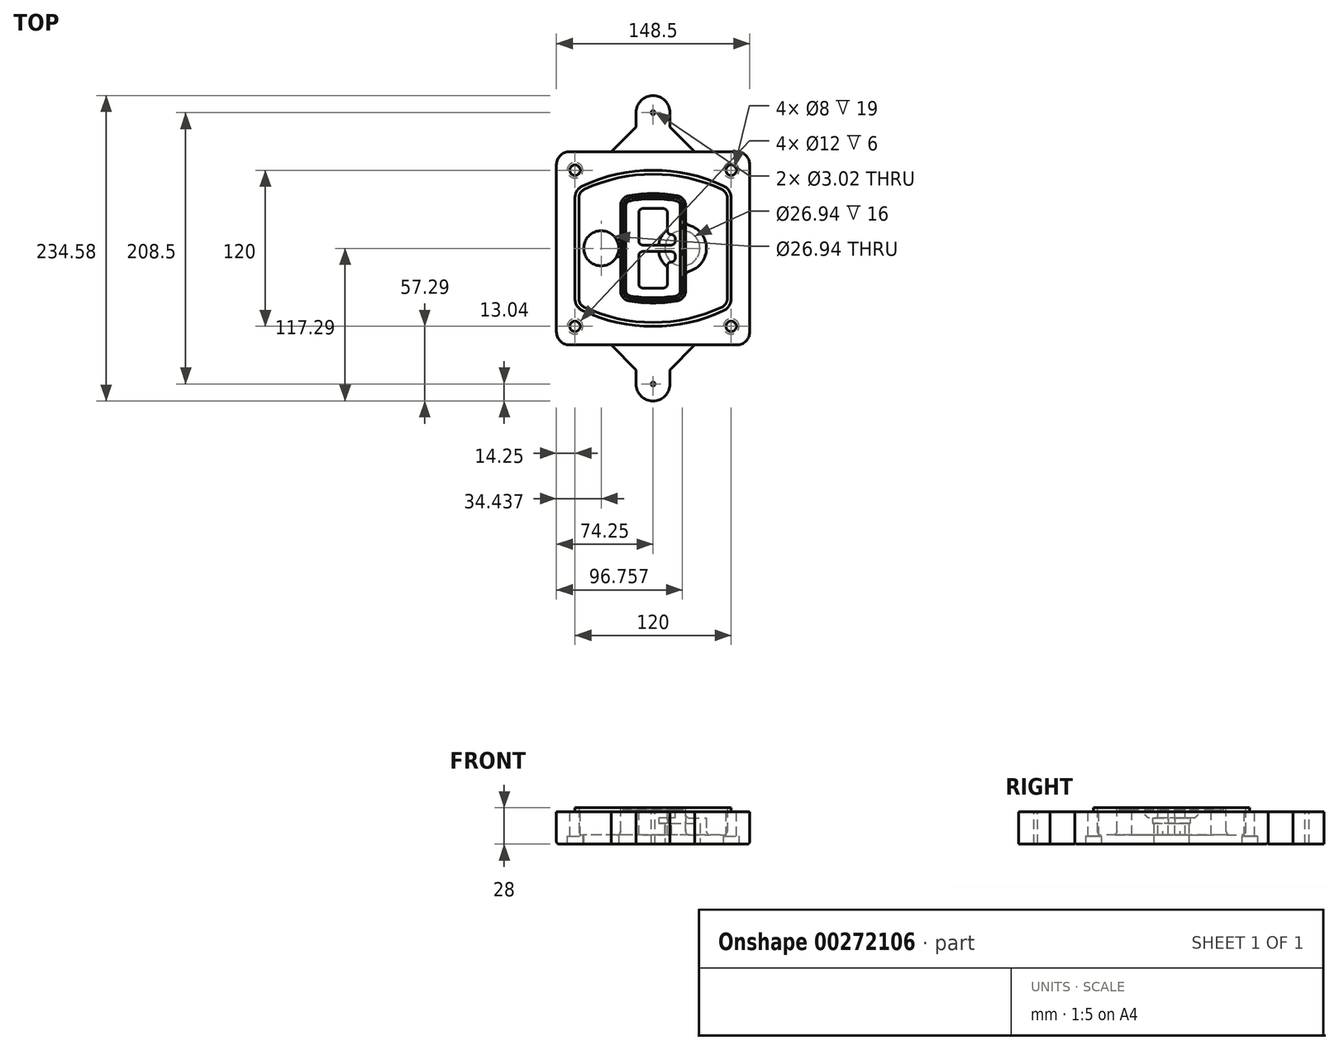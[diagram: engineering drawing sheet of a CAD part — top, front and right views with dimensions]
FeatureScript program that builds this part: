
annotation { "Feature Type Name" : "Feature", "Feature Type Description" : "" }
export const myFeature = defineFeature(function(context is Context, id is Id, definition is map)
    precondition{}
    {
        {
            var Q0;
            Q0=qCreatedBy(makeId("Top.planeOp"),FACE);
            var sketch = newSketch(context, id + "F0", { "sketchPlane" : qUnion([Q0])});
            skPoint(sketch, "E0.rect.middle", {"position": v(0, 0) * mm});
            skLineSegment(sketch, "E1.bottom", {"start": v(-64.25, -74.25) * mm, "end": v(64.25, -74.25) * mm});
            skLineSegment(sketch, "E1.top", {"start": v(-64.25, 74.25) * mm, "end": v(64.25, 74.25) * mm});
            skLineSegment(sketch, "E1.left", {"start": v(-74.25, -64.25) * mm, "end": v(-74.25, 64.25) * mm});
            skLineSegment(sketch, "E1.right", {"start": v(74.25, -64.25) * mm, "end": v(74.25, 64.25) * mm});
            skLineSegment(sketch, "E2", {"start": v(-74.25, 74.25) * mm, "end": v(74.25, -74.25) * mm, "construction": true});
            skLineSegment(sketch, "E3", {"start": v(74.25, 74.25) * mm, "end": v(-74.25, -74.25) * mm, "construction": true});
            skCircle(sketch, "E4", {"center": v(-60, 60) * mm, "radius": 4 * mm});
            skCircle(sketch, "E5", {"center": v(60, 60) * mm, "radius": 4 * mm});
            skCircle(sketch, "E6", {"center": v(60, -60) * mm, "radius": 4 * mm});
            skCircle(sketch, "E7", {"center": v(-60, -60) * mm, "radius": 4 * mm});
            skLineSegment(sketch, "E8", {"start": v(-60, 60) * mm, "end": v(60, 60) * mm, "construction": true});
            skLineSegment(sketch, "E9", {"start": v(60, 60) * mm, "end": v(60, -60) * mm, "construction": true});
            skLineSegment(sketch, "E10", {"start": v(60, -60) * mm, "end": v(-60, -60) * mm, "construction": true});
            skLineSegment(sketch, "E11", {"start": v(-60, -60) * mm, "end": v(-60, 60) * mm, "construction": true});
            skLineSegment(sketch, "E12", {"start": v(-60, 38.83) * mm, "end": v(-60, -38.83) * mm});
            skLineSegment(sketch, "E13", {"start": v(60, 38.83) * mm, "end": v(60, -38.83) * mm});
            skArc(sketch, "E14", {"start": v(54.26, 47.88) * mm, "mid": v(0, 60) * mm, "end": v(-54.26, 47.88) * mm});
            skArc(sketch, "E15", {"start": v(-54.26, -47.88) * mm, "mid": v(0, -60) * mm, "end": v(54.26, -47.88) * mm});
            skLineSegment(sketch, "E16", {"start": v(-60, 0) * mm, "end": v(60, 0) * mm, "construction": true});
            skPoint(sketch, "E17.visualSharp", {"position": v(-60, -45) * mm});
            skArc(sketch, "E17.filletArc", {"start": v(-60, -38.83) * mm, "mid": v(-58.44, -44.2) * mm, "end": v(-54.26, -47.88) * mm});
            skPoint(sketch, "E18.visualSharp", {"position": v(-60, 45) * mm});
            skArc(sketch, "E18.filletArc", {"start": v(-54.26, 47.88) * mm, "mid": v(-58.44, 44.2) * mm, "end": v(-60, 38.83) * mm});
            skPoint(sketch, "E19.visualSharp", {"position": v(60, 45) * mm});
            skArc(sketch, "E19.filletArc", {"start": v(60, 38.83) * mm, "mid": v(58.44, 44.2) * mm, "end": v(54.26, 47.88) * mm});
            skPoint(sketch, "E20.visualSharp", {"position": v(60, -45) * mm});
            skArc(sketch, "E20.filletArc", {"start": v(54.26, -47.88) * mm, "mid": v(58.44, -44.2) * mm, "end": v(60, -38.83) * mm});
            skPoint(sketch, "E21.visualSharp", {"position": v(-74.25, 74.25) * mm});
            skArc(sketch, "E21.filletArc", {"start": v(-64.25, 74.25) * mm, "mid": v(-71.32, 71.32) * mm, "end": v(-74.25, 64.25) * mm});
            skPoint(sketch, "E22.visualSharp", {"position": v(74.25, 74.25) * mm});
            skArc(sketch, "E22.filletArc", {"start": v(74.25, 64.25) * mm, "mid": v(71.32, 71.32) * mm, "end": v(64.25, 74.25) * mm});
            skPoint(sketch, "E23.visualSharp", {"position": v(74.25, -74.25) * mm});
            skArc(sketch, "E23.filletArc", {"start": v(64.25, -74.25) * mm, "mid": v(71.32, -71.32) * mm, "end": v(74.25, -64.25) * mm});
            skPoint(sketch, "E24.visualSharp", {"position": v(-74.25, -74.25) * mm});
            skArc(sketch, "E24.filletArc", {"start": v(-74.25, -64.25) * mm, "mid": v(-71.32, -71.32) * mm, "end": v(-64.25, -74.25) * mm});
            skArc(sketch, "E25.0", {"start": v(57, 38.83) * mm, "mid": v(55.9, 42.58) * mm, "end": v(52.98, 45.17) * mm});
            skLineSegment(sketch, "E25.1", {"start": v(57, 38.83) * mm, "end": v(57, -38.83) * mm});
            skArc(sketch, "E25.2", {"start": v(52.98, -45.17) * mm, "mid": v(55.9, -42.58) * mm, "end": v(57, -38.83) * mm});
            skArc(sketch, "E25.3", {"start": v(-52.98, -45.17) * mm, "mid": v(0, -57) * mm, "end": v(52.98, -45.17) * mm});
            skArc(sketch, "E25.4", {"start": v(-57, -38.83) * mm, "mid": v(-55.9, -42.58) * mm, "end": v(-52.98, -45.17) * mm});
            skArc(sketch, "E25.5", {"start": v(52.98, 45.17) * mm, "mid": v(0, 57) * mm, "end": v(-52.98, 45.17) * mm});
            skLineSegment(sketch, "E25.6", {"start": v(-57, 38.83) * mm, "end": v(-57, -38.83) * mm});
            skArc(sketch, "E25.7", {"start": v(-52.98, 45.17) * mm, "mid": v(-55.9, 42.58) * mm, "end": v(-57, 38.83) * mm});
            skArc(sketch, "E26.0", {"start": v(-55.96, 51.5) * mm, "mid": v(-61.82, 46.33) * mm, "end": v(-64, 38.83) * mm});
            skArc(sketch, "E26.1", {"start": v(55.96, 51.5) * mm, "mid": v(0, 64) * mm, "end": v(-55.96, 51.5) * mm});
            skArc(sketch, "E26.2", {"start": v(64, 38.83) * mm, "mid": v(61.82, 46.33) * mm, "end": v(55.96, 51.5) * mm});
            skLineSegment(sketch, "E26.3", {"start": v(64, 38.83) * mm, "end": v(64, -38.83) * mm});
            skArc(sketch, "E26.4", {"start": v(55.96, -51.5) * mm, "mid": v(61.82, -46.33) * mm, "end": v(64, -38.83) * mm});
            skLineSegment(sketch, "E26.5", {"start": v(-64, 38.83) * mm, "end": v(-64, -38.83) * mm});
            skArc(sketch, "E26.6", {"start": v(-55.96, -51.5) * mm, "mid": v(0, -64) * mm, "end": v(55.96, -51.5) * mm});
            skArc(sketch, "E26.7", {"start": v(-64, -38.83) * mm, "mid": v(-61.82, -46.33) * mm, "end": v(-55.96, -51.5) * mm});
            skSolve(sketch);
        }
        {
            var Q0;
            Q0=makeQuery(id+"F0.imprint","IMPRINT",FACE,{"disambiguationData":[TD([[makeQuery(id+"F0.imprint","IMPRINT",EDGE,{"derivedFrom":sQuery(id+"F0.wireOp",EDGE,"E1.bottom")}),1.0]])]});
            var Q1;
            Q1=makeQuery(id+"F0.imprint","IMPRINT",FACE,{"disambiguationData":[TD([[makeQuery(id+"F0.imprint","IMPRINT",EDGE,{"derivedFrom":sQuery(id+"F0.wireOp",EDGE,"E12")}),1.0]])]});
            var Q2;
            Q2=makeQuery(id+"F0.imprint","IMPRINT",FACE,{"disambiguationData":[TD([[makeQuery(id+"F0.imprint","IMPRINT",EDGE,{"derivedFrom":sQuery(id+"F0.wireOp",EDGE,"E25.0")}),1.0]])]});
            var Q3;
            Q3=makeQuery(id+"F0.imprint","IMPRINT",FACE,{"disambiguationData":[TD([[makeQuery(id+"F0.imprint","IMPRINT",EDGE,{"derivedFrom":sQuery(id+"F0.wireOp",EDGE,"E12")}),-1.0]])]});
            extrude(context, id + "F1", {"entities" : qUnion([Q0, Q1, Q2, Q3]), "oppositeDirection" : true, "depth" : 25 * mm});
        }
        {
            var Q0;
            Q0=makeQuery(id+"F0.imprint","IMPRINT",FACE,{"disambiguationData":[TD([[makeQuery(id+"F0.imprint","IMPRINT",EDGE,{"derivedFrom":sQuery(id+"F0.wireOp",EDGE,"E12")}),1.0]])]});
            extrude(context, id + "F2", {"entities" : qUnion([Q0]), "operationType" : NewBodyOperationType.ADD, "depth" : 3 * mm});
        }
        {
            var Q0;
            Q0=makeQuery(id+"F0.imprint","IMPRINT",FACE,{"disambiguationData":[TD([[makeQuery(id+"F0.imprint","IMPRINT",EDGE,{"derivedFrom":sQuery(id+"F0.wireOp",EDGE,"E25.0")}),1.0]])]});
            extrude(context, id + "F3", {"entities" : qUnion([Q0]), "operationType" : NewBodyOperationType.REMOVE, "oppositeDirection" : true, "depth" : 18 * mm});
        }
        {
            var Q0;
            Q0=makeQuery(id+"F2.opExtrude","CAP_FACE",FACE,{"disambiguationData":[OSD([sQuery(id+"F0.wireOp",EDGE,"E12"),sQuery(id+"F0.wireOp",EDGE,"E13"),sQuery(id+"F0.wireOp",EDGE,"E14"),sQuery(id+"F0.wireOp",EDGE,"E15"),sQuery(id+"F0.wireOp",EDGE,"E17.filletArc"),sQuery(id+"F0.wireOp",EDGE,"E18.filletArc"),sQuery(id+"F0.wireOp",EDGE,"E19.filletArc"),sQuery(id+"F0.wireOp",EDGE,"E20.filletArc"),sQuery(id+"F0.wireOp",EDGE,"E25.0"),sQuery(id+"F0.wireOp",EDGE,"E25.1"),sQuery(id+"F0.wireOp",EDGE,"E25.2"),sQuery(id+"F0.wireOp",EDGE,"E25.3"),sQuery(id+"F0.wireOp",EDGE,"E25.4"),sQuery(id+"F0.wireOp",EDGE,"E25.5"),sQuery(id+"F0.wireOp",EDGE,"E25.6"),sQuery(id+"F0.wireOp",EDGE,"E25.7")])],"isStart":false});
            var sketch = newSketch(context, id + "F4", { "sketchPlane" : qUnion([Q0])});
            skArc(sketch, "E27.0", {"start": v(-18.34, -40.45) * mm, "mid": v(0, -42) * mm, "end": v(18.34, -40.45) * mm});
            skArc(sketch, "E28.0", {"start": v(18.34, 40.45) * mm, "mid": v(0, 42) * mm, "end": v(-18.34, 40.45) * mm});
            skLineSegment(sketch, "E29", {"start": v(-25, 32.57) * mm, "end": v(-25, -32.57) * mm});
            skLineSegment(sketch, "E30", {"start": v(25, 32.57) * mm, "end": v(25, -32.57) * mm});
            skLineSegment(sketch, "E31", {"start": v(-25, 39.1) * mm, "end": v(25, 39.1) * mm, "construction": true});
            skLineSegment(sketch, "E32", {"start": v(-25, -39.1) * mm, "end": v(25, -39.1) * mm, "construction": true});
            skPoint(sketch, "E33.visualSharp", {"position": v(-25, 39.1) * mm});
            skArc(sketch, "E33.filletArc", {"start": v(-18.34, 40.45) * mm, "mid": v(-23.11, 37.73) * mm, "end": v(-25, 32.57) * mm});
            skPoint(sketch, "E34.visualSharp", {"position": v(25, 39.1) * mm});
            skArc(sketch, "E34.filletArc", {"start": v(25, 32.57) * mm, "mid": v(23.11, 37.73) * mm, "end": v(18.34, 40.45) * mm});
            skPoint(sketch, "E35.visualSharp", {"position": v(25, -39.1) * mm});
            skArc(sketch, "E35.filletArc", {"start": v(18.34, -40.45) * mm, "mid": v(23.11, -37.73) * mm, "end": v(25, -32.57) * mm});
            skPoint(sketch, "E36.visualSharp", {"position": v(-25, -39.1) * mm});
            skArc(sketch, "E36.filletArc", {"start": v(-25, -32.57) * mm, "mid": v(-23.11, -37.73) * mm, "end": v(-18.34, -40.45) * mm});
            skArc(sketch, "E37.0", {"start": v(52.98, 45.17) * mm, "mid": v(0, 57) * mm, "end": v(-52.98, 45.17) * mm});
            skArc(sketch, "E37.1", {"start": v(-52.98, 45.17) * mm, "mid": v(-55.9, 42.58) * mm, "end": v(-57, 38.83) * mm});
            skLineSegment(sketch, "E37.2", {"start": v(-57, 38.83) * mm, "end": v(-57, -38.83) * mm});
            skArc(sketch, "E37.3", {"start": v(-57, -38.83) * mm, "mid": v(-55.9, -42.58) * mm, "end": v(-52.98, -45.17) * mm});
            skArc(sketch, "E37.4", {"start": v(-52.98, -45.17) * mm, "mid": v(0, -57) * mm, "end": v(52.98, -45.17) * mm});
            skArc(sketch, "E37.5", {"start": v(52.98, -45.17) * mm, "mid": v(55.9, -42.58) * mm, "end": v(57, -38.83) * mm});
            skLineSegment(sketch, "E37.6", {"start": v(57, 38.83) * mm, "end": v(57, -38.83) * mm});
            skArc(sketch, "E37.7", {"start": v(57, 38.83) * mm, "mid": v(55.9, 42.58) * mm, "end": v(52.98, 45.17) * mm});
            skLineSegment(sketch, "E38.0", {"start": v(23, 32.57) * mm, "end": v(23, -32.57) * mm});
            skArc(sketch, "E38.1", {"start": v(18, -38.48) * mm, "mid": v(21.58, -36.44) * mm, "end": v(23, -32.57) * mm});
            skArc(sketch, "E38.2", {"start": v(-18, -38.48) * mm, "mid": v(0, -40) * mm, "end": v(18, -38.48) * mm});
            skArc(sketch, "E38.3", {"start": v(-23, -32.57) * mm, "mid": v(-21.58, -36.44) * mm, "end": v(-18, -38.48) * mm});
            skLineSegment(sketch, "E38.4", {"start": v(-23, 32.57) * mm, "end": v(-23, -32.57) * mm});
            skArc(sketch, "E38.5", {"start": v(23, 32.57) * mm, "mid": v(21.58, 36.44) * mm, "end": v(18, 38.48) * mm});
            skArc(sketch, "E38.6", {"start": v(-18, 38.48) * mm, "mid": v(-21.58, 36.44) * mm, "end": v(-23, 32.57) * mm});
            skArc(sketch, "E38.7", {"start": v(18, 38.48) * mm, "mid": v(0, 40) * mm, "end": v(-18, 38.48) * mm});
            skArc(sketch, "E39.0", {"start": v(21, 32.57) * mm, "mid": v(20.06, 35.15) * mm, "end": v(17.67, 36.5) * mm});
            skLineSegment(sketch, "E39.1", {"start": v(21, 32.57) * mm, "end": v(21, -32.57) * mm});
            skArc(sketch, "E39.2", {"start": v(17.67, -36.5) * mm, "mid": v(20.06, -35.15) * mm, "end": v(21, -32.57) * mm});
            skArc(sketch, "E39.3", {"start": v(-17.67, -36.5) * mm, "mid": v(0, -38) * mm, "end": v(17.67, -36.5) * mm});
            skArc(sketch, "E39.4", {"start": v(-21, -32.57) * mm, "mid": v(-20.06, -35.15) * mm, "end": v(-17.67, -36.5) * mm});
            skArc(sketch, "E39.5", {"start": v(17.67, 36.5) * mm, "mid": v(0, 38) * mm, "end": v(-17.67, 36.5) * mm});
            skLineSegment(sketch, "E39.6", {"start": v(-21, 32.57) * mm, "end": v(-21, -32.57) * mm});
            skArc(sketch, "E39.7", {"start": v(-17.67, 36.5) * mm, "mid": v(-20.06, 35.15) * mm, "end": v(-21, 32.57) * mm});
            skLineSegment(sketch, "E40", {"start": v(-25, 0) * mm, "end": v(25, 0) * mm, "construction": true});
            skLineSegment(sketch, "E41", {"start": v(-11, 5.5) * mm, "end": v(-11, 27.5) * mm});
            skLineSegment(sketch, "E42", {"start": v(-8, 30.5) * mm, "end": v(8, 30.5) * mm});
            skLineSegment(sketch, "E43", {"start": v(11, 27.5) * mm, "end": v(11, 13.5) * mm});
            skLineSegment(sketch, "E44", {"start": v(14, 10.5) * mm, "end": v(14, 10.5) * mm});
            skLineSegment(sketch, "E45", {"start": v(17, 7.5) * mm, "end": v(17, 5.5) * mm});
            skLineSegment(sketch, "E46", {"start": v(14, 2.5) * mm, "end": v(-8, 2.5) * mm});
            skPoint(sketch, "E47.visualSharp", {"position": v(-11, 30.5) * mm});
            skArc(sketch, "E47.filletArc", {"start": v(-8, 30.5) * mm, "mid": v(-10.12, 29.62) * mm, "end": v(-11, 27.5) * mm});
            skPoint(sketch, "E48.visualSharp", {"position": v(11, 30.5) * mm});
            skArc(sketch, "E48.filletArc", {"start": v(11, 27.5) * mm, "mid": v(10.12, 29.62) * mm, "end": v(8, 30.5) * mm});
            skPoint(sketch, "E49.visualSharp", {"position": v(11, 10.5) * mm});
            skArc(sketch, "E49.filletArc", {"start": v(11, 13.5) * mm, "mid": v(11.88, 11.38) * mm, "end": v(14, 10.5) * mm});
            skPoint(sketch, "E50.visualSharp", {"position": v(17, 10.5) * mm});
            skArc(sketch, "E50.filletArc", {"start": v(17, 7.5) * mm, "mid": v(16.12, 9.62) * mm, "end": v(14, 10.5) * mm});
            skPoint(sketch, "E51.visualSharp", {"position": v(17, 2.5) * mm});
            skArc(sketch, "E51.filletArc", {"start": v(14, 2.5) * mm, "mid": v(16.12, 3.38) * mm, "end": v(17, 5.5) * mm});
            skPoint(sketch, "E52.visualSharp", {"position": v(-11, 2.5) * mm});
            skArc(sketch, "E52.filletArc", {"start": v(-11, 5.5) * mm, "mid": v(-10.12, 3.38) * mm, "end": v(-8, 2.5) * mm});
            skLineSegment(sketch, "E53.0.MirrorCS", {"start": v(14, -2.5) * mm, "end": v(-8, -2.5) * mm});
            skArc(sketch, "E54.0.MirrorCS", {"start": v(-11, -5.5) * mm, "mid": v(-10.12, -3.38) * mm, "end": v(-8, -2.5) * mm});
            skLineSegment(sketch, "E55.0.MirrorCS", {"start": v(-11, -5.5) * mm, "end": v(-11, -27.5) * mm});
            skArc(sketch, "E56.0.MirrorCS", {"start": v(-8, -30.5) * mm, "mid": v(-10.12, -29.62) * mm, "end": v(-11, -27.5) * mm});
            skLineSegment(sketch, "E57.0.MirrorCS", {"start": v(-8, -30.5) * mm, "end": v(8, -30.5) * mm});
            skArc(sketch, "E58.0.MirrorCS", {"start": v(11, -27.5) * mm, "mid": v(10.12, -29.62) * mm, "end": v(8, -30.5) * mm});
            skLineSegment(sketch, "E59.0.MirrorCS", {"start": v(11, -27.5) * mm, "end": v(11, -13.5) * mm});
            skArc(sketch, "E60.0.MirrorCS", {"start": v(11, -13.5) * mm, "mid": v(11.88, -11.38) * mm, "end": v(14, -10.5) * mm});
            skArc(sketch, "E61.0.MirrorCS", {"start": v(17, -7.5) * mm, "mid": v(16.12, -9.62) * mm, "end": v(14, -10.5) * mm});
            skLineSegment(sketch, "E62.0.MirrorCS", {"start": v(17, -7.5) * mm, "end": v(17, -5.5) * mm});
            skArc(sketch, "E63.0.MirrorCS", {"start": v(14, -2.5) * mm, "mid": v(16.12, -3.38) * mm, "end": v(17, -5.5) * mm});
            skSolve(sketch);
        }
        {
            var Q0;
            Q0=makeQuery(id+"F4.imprint","IMPRINT",FACE,{"disambiguationData":[TD([[makeQuery(id+"F4.imprint","IMPRINT",EDGE,{"derivedFrom":sQuery(id+"F4.wireOp",EDGE,"E27.0")}),1.0]])]});
            var Q1;
            Q1=makeQuery(id+"F4.imprint","IMPRINT",FACE,{"disambiguationData":[TD([[makeQuery(id+"F4.imprint","IMPRINT",EDGE,{"derivedFrom":sQuery(id+"F4.wireOp",EDGE,"E38.0")}),-1.0]])]});
            var Q2;
            Q2=makeQuery(id+"F4.imprint","IMPRINT",FACE,{"disambiguationData":[TD([[makeQuery(id+"F4.imprint","IMPRINT",EDGE,{"derivedFrom":sQuery(id+"F4.wireOp",EDGE,"E39.0")}),1.0]])]});
            extrude(context, id + "F5", {"entities" : qUnion([Q0, Q1, Q2]), "operationType" : NewBodyOperationType.ADD, "endBound" : BoundingType.UP_TO_NEXT, "oppositeDirection" : true, "depth" : 25 * mm});
        }
        {
            var Q0;
            Q0=makeQuery(id+"F4.imprint","IMPRINT",FACE,{"disambiguationData":[TD([[makeQuery(id+"F4.imprint","IMPRINT",EDGE,{"derivedFrom":sQuery(id+"F4.wireOp",EDGE,"E38.0")}),-1.0]])]});
            extrude(context, id + "F6", {"entities" : qUnion([Q0]), "operationType" : NewBodyOperationType.REMOVE, "oppositeDirection" : true, "depth" : 2 * mm});
        }
        {
            var Q0;
            Q0=makeQuery(id+"F1.opExtrude","CAP_FACE",FACE,{"disambiguationData":[OSD([sQuery(id+"F0.wireOp",EDGE,"E1.bottom"),sQuery(id+"F0.wireOp",EDGE,"E1.top"),sQuery(id+"F0.wireOp",EDGE,"E1.left"),sQuery(id+"F0.wireOp",EDGE,"E1.right"),sQuery(id+"F0.wireOp",EDGE,"E4"),sQuery(id+"F0.wireOp",EDGE,"E5"),sQuery(id+"F0.wireOp",EDGE,"E6"),sQuery(id+"F0.wireOp",EDGE,"E7"),sQuery(id+"F0.wireOp",EDGE,"E21.filletArc"),sQuery(id+"F0.wireOp",EDGE,"E22.filletArc"),sQuery(id+"F0.wireOp",EDGE,"E23.filletArc"),sQuery(id+"F0.wireOp",EDGE,"E24.filletArc")])],"isStart":false});
            var sketch = newSketch(context, id + "F7", { "sketchPlane" : qUnion([Q0])});
            skCircle(sketch, "E64", {"center": v(22.5, 0) * mm, "radius": 13.47 * mm});
            skCircle(sketch, "E65", {"center": v(-39.81, 0) * mm, "radius": 13.47 * mm});
            skLineSegment(sketch, "E66", {"start": v(74.25, 0) * mm, "end": v(-74.25, 0) * mm});
            skCircle(sketch, "E67", {"center": v(22.5, 0) * mm, "radius": 18.47 * mm});
            skCircle(sketch, "E68", {"center": v(60, -60) * mm, "radius": 6 * mm});
            skCircle(sketch, "E69", {"center": v(-60, -60) * mm, "radius": 6 * mm});
            skCircle(sketch, "E70", {"center": v(-60, 60) * mm, "radius": 6 * mm});
            skCircle(sketch, "E71", {"center": v(60, 60) * mm, "radius": 6 * mm});
            skSolve(sketch);
        }
        {
            var Q0;
            {var subQ1=sQuery(id+"F7.wireOp",EDGE,"E66");var subQ4=sQuery(id+"F7.wireOp",EDGE,"E64");var subQ6=makeQuery(id+"F7.imprint","INTERSECT",VERTEX,{"disambiguationData":[OD(0.0)],"derivedFrom":[subQ4,subQ1]});Q0=makeQuery(id+"F7.imprint","IMPRINT",FACE,{"disambiguationData":[TD([[makeQuery(id+"F7.imprint","IMPRINT",EDGE,{"disambiguationData":[TD([[subQ6,-1.0]])],"derivedFrom":subQ4}),-1.0]])]});}
            var Q1;
            {var subQ0=sQuery(id+"F7.wireOp",EDGE,"E66");var subQ1=sQuery(id+"F7.wireOp",EDGE,"E64");var subQ3=makeQuery(id+"F7.imprint","INTERSECT",VERTEX,{"disambiguationData":[OD(0.0)],"derivedFrom":[subQ1,subQ0]});Q1=makeQuery(id+"F7.imprint","IMPRINT",FACE,{"disambiguationData":[TD([[makeQuery(id+"F7.imprint","IMPRINT",EDGE,{"disambiguationData":[TD([[subQ3,-1.0]])],"derivedFrom":subQ1}),1.0]])]});}
            var Q2;
            {var subQ0=sQuery(id+"F7.wireOp",EDGE,"E66");var subQ1=sQuery(id+"F7.wireOp",EDGE,"E64");var subQ3=makeQuery(id+"F7.imprint","INTERSECT",VERTEX,{"disambiguationData":[OD(0.0)],"derivedFrom":[subQ1,subQ0]});Q2=makeQuery(id+"F7.imprint","IMPRINT",FACE,{"disambiguationData":[TD([[makeQuery(id+"F7.imprint","IMPRINT",EDGE,{"disambiguationData":[TD([[subQ3,1.0]])],"derivedFrom":subQ1}),1.0]])]});}
            var Q3;
            {var subQ1=sQuery(id+"F7.wireOp",EDGE,"E66");var subQ4=sQuery(id+"F7.wireOp",EDGE,"E64");var subQ6=makeQuery(id+"F7.imprint","INTERSECT",VERTEX,{"disambiguationData":[OD(0.0)],"derivedFrom":[subQ4,subQ1]});Q3=makeQuery(id+"F7.imprint","IMPRINT",FACE,{"disambiguationData":[TD([[makeQuery(id+"F7.imprint","IMPRINT",EDGE,{"disambiguationData":[TD([[subQ6,1.0]])],"derivedFrom":subQ4}),-1.0]])]});}
            extrude(context, id + "F8", {"entities" : qUnion([Q0, Q1, Q2, Q3]), "operationType" : NewBodyOperationType.ADD, "oppositeDirection" : true, "depth" : 20 * mm});
        }
        {
            var Q0;
            {var subQ0=sQuery(id+"F7.wireOp",EDGE,"E66");var subQ1=sQuery(id+"F7.wireOp",EDGE,"E64");var subQ3=makeQuery(id+"F7.imprint","INTERSECT",VERTEX,{"disambiguationData":[OD(0.0)],"derivedFrom":[subQ1,subQ0]});Q0=makeQuery(id+"F7.imprint","IMPRINT",FACE,{"disambiguationData":[TD([[makeQuery(id+"F7.imprint","IMPRINT",EDGE,{"disambiguationData":[TD([[subQ3,-1.0]])],"derivedFrom":subQ1}),1.0]])]});}
            var Q1;
            {var subQ0=sQuery(id+"F7.wireOp",EDGE,"E66");var subQ1=sQuery(id+"F7.wireOp",EDGE,"E64");var subQ3=makeQuery(id+"F7.imprint","INTERSECT",VERTEX,{"disambiguationData":[OD(0.0)],"derivedFrom":[subQ1,subQ0]});Q1=makeQuery(id+"F7.imprint","IMPRINT",FACE,{"disambiguationData":[TD([[makeQuery(id+"F7.imprint","IMPRINT",EDGE,{"disambiguationData":[TD([[subQ3,1.0]])],"derivedFrom":subQ1}),1.0]])]});}
            extrude(context, id + "F9", {"entities" : qUnion([Q0, Q1]), "operationType" : NewBodyOperationType.REMOVE, "oppositeDirection" : true, "depth" : 16 * mm});
        }
        {
            var Q0;
            {var subQ0=sQuery(id+"F7.wireOp",EDGE,"E66");var subQ1=sQuery(id+"F7.wireOp",EDGE,"E65");var subQ3=makeQuery(id+"F7.imprint","INTERSECT",VERTEX,{"disambiguationData":[OD(0.0)],"derivedFrom":[subQ1,subQ0]});Q0=makeQuery(id+"F7.imprint","IMPRINT",FACE,{"disambiguationData":[TD([[makeQuery(id+"F7.imprint","IMPRINT",EDGE,{"disambiguationData":[TD([[subQ3,-1.0]])],"derivedFrom":subQ1}),1.0]])]});}
            var Q1;
            {var subQ0=sQuery(id+"F7.wireOp",EDGE,"E66");var subQ1=sQuery(id+"F7.wireOp",EDGE,"E65");var subQ3=makeQuery(id+"F7.imprint","INTERSECT",VERTEX,{"disambiguationData":[OD(0.0)],"derivedFrom":[subQ1,subQ0]});Q1=makeQuery(id+"F7.imprint","IMPRINT",FACE,{"disambiguationData":[TD([[makeQuery(id+"F7.imprint","IMPRINT",EDGE,{"disambiguationData":[TD([[subQ3,1.0]])],"derivedFrom":subQ1}),1.0]])]});}
            extrude(context, id + "F10", {"entities" : qUnion([Q0, Q1]), "operationType" : NewBodyOperationType.REMOVE, "oppositeDirection" : true, "depth" : 25 * mm});
        }
        {
            var Q0;
            Q0=makeQuery(id+"F7.imprint","IMPRINT",FACE,{"disambiguationData":[TD([[makeQuery(id+"F7.imprint","IMPRINT",EDGE,{"derivedFrom":sQuery(id+"F7.wireOp",EDGE,"E68")}),1.0]])]});
            var Q1;
            Q1=makeQuery(id+"F7.imprint","IMPRINT",FACE,{"disambiguationData":[TD([[makeQuery(id+"F7.imprint","IMPRINT",EDGE,{"derivedFrom":makeQuery(id+"F1.opExtrude","CAP_EDGE",EDGE,{"disambiguationData":[OSD([sQuery(id+"F0.wireOp",EDGE,"E5")])],"isStart":false})}),-1.0]])]});
            var Q2;
            Q2=makeQuery(id+"F7.imprint","IMPRINT",FACE,{"disambiguationData":[TD([[makeQuery(id+"F7.imprint","IMPRINT",EDGE,{"derivedFrom":sQuery(id+"F7.wireOp",EDGE,"E69")}),1.0]])]});
            var Q3;
            Q3=makeQuery(id+"F7.imprint","IMPRINT",FACE,{"disambiguationData":[TD([[makeQuery(id+"F7.imprint","IMPRINT",EDGE,{"derivedFrom":makeQuery(id+"F1.opExtrude","CAP_EDGE",EDGE,{"disambiguationData":[OSD([sQuery(id+"F0.wireOp",EDGE,"E4")])],"isStart":false})}),-1.0]])]});
            var Q4;
            Q4=makeQuery(id+"F7.imprint","IMPRINT",FACE,{"disambiguationData":[TD([[makeQuery(id+"F7.imprint","IMPRINT",EDGE,{"derivedFrom":sQuery(id+"F7.wireOp",EDGE,"E70")}),1.0]])]});
            var Q5;
            Q5=makeQuery(id+"F7.imprint","IMPRINT",FACE,{"disambiguationData":[TD([[makeQuery(id+"F7.imprint","IMPRINT",EDGE,{"derivedFrom":makeQuery(id+"F1.opExtrude","CAP_EDGE",EDGE,{"disambiguationData":[OSD([sQuery(id+"F0.wireOp",EDGE,"E7")])],"isStart":false})}),-1.0]])]});
            var Q6;
            Q6=makeQuery(id+"F7.imprint","IMPRINT",FACE,{"disambiguationData":[TD([[makeQuery(id+"F7.imprint","IMPRINT",EDGE,{"derivedFrom":sQuery(id+"F7.wireOp",EDGE,"E71")}),1.0]])]});
            var Q7;
            Q7=makeQuery(id+"F7.imprint","IMPRINT",FACE,{"disambiguationData":[TD([[makeQuery(id+"F7.imprint","IMPRINT",EDGE,{"derivedFrom":makeQuery(id+"F1.opExtrude","CAP_EDGE",EDGE,{"disambiguationData":[OSD([sQuery(id+"F0.wireOp",EDGE,"E6")])],"isStart":false})}),-1.0]])]});
            extrude(context, id + "F11", {"entities" : qUnion([Q0, Q1, Q2, Q3, Q4, Q5, Q6, Q7]), "operationType" : NewBodyOperationType.REMOVE, "oppositeDirection" : true, "depth" : 6 * mm});
        }
        {
            var Q0;
            Q0=makeQuery(id+"F9.boolean.opBoolean","COPY",FACE,{"derivedFrom":makeQuery(id+"F9.opExtrude","CAP_FACE",FACE,{"disambiguationData":[OSD([sQuery(id+"F7.wireOp",EDGE,"E64")])],"isStart":false})});
            var sketch = newSketch(context, id + "F12", { "sketchPlane" : qUnion([Q0])});
            skArc(sketch, "E72.0", {"start": v(11, 14.45) * mm, "mid": v(6.45, 9.13) * mm, "end": v(4.2, 2.5) * mm});
            skArc(sketch, "E72.1", {"start": v(4.2, -2.5) * mm, "mid": v(6.45, -9.13) * mm, "end": v(11, -14.45) * mm});
            skLineSegment(sketch, "E73", {"start": v(4.2, -2.5) * mm, "end": v(14, -2.5) * mm});
            skLineSegment(sketch, "E74.0", {"start": v(14, 2.5) * mm, "end": v(4.2, 2.5) * mm});
            skArc(sketch, "E74.1", {"start": v(14, 2.5) * mm, "mid": v(16.12, 3.38) * mm, "end": v(17, 5.5) * mm});
            skLineSegment(sketch, "E74.2", {"start": v(17, 7.5) * mm, "end": v(17, 5.5) * mm});
            skArc(sketch, "E74.3", {"start": v(17, 7.5) * mm, "mid": v(16.12, 9.62) * mm, "end": v(14, 10.5) * mm});
            skArc(sketch, "E74.4", {"start": v(11, 13.5) * mm, "mid": v(11.88, 11.38) * mm, "end": v(14, 10.5) * mm});
            skLineSegment(sketch, "E74.5", {"start": v(11, 14.45) * mm, "end": v(11, 13.5) * mm});
            skLineSegment(sketch, "E74.7", {"start": v(14, -2.5) * mm, "end": v(4.2, -2.5) * mm});
            skArc(sketch, "E74.8", {"start": v(14, -2.5) * mm, "mid": v(16.12, -3.38) * mm, "end": v(17, -5.5) * mm});
            skLineSegment(sketch, "E74.9", {"start": v(17, -7.5) * mm, "end": v(17, -5.5) * mm});
            skArc(sketch, "E74.10", {"start": v(17, -7.5) * mm, "mid": v(16.12, -9.62) * mm, "end": v(14, -10.5) * mm});
            skArc(sketch, "E74.11", {"start": v(11, -13.5) * mm, "mid": v(11.88, -11.38) * mm, "end": v(14, -10.5) * mm});
            skLineSegment(sketch, "E74.12", {"start": v(11, -14.45) * mm, "end": v(11, -13.5) * mm});
            skPoint(sketch, "E75.orphan", {"position": v(11, -27.5) * mm});
            skPoint(sketch, "E76.orphan", {"position": v(-8, -2.5) * mm});
            skPoint(sketch, "E77.orphan", {"position": v(-8, 2.5) * mm});
            skPoint(sketch, "E78.orphan", {"position": v(11, 27.5) * mm});
            skSolve(sketch);
        }
        {
            var Q0;
            {var subQ7=sQuery(id+"F12.wireOp",EDGE,"E72.0");var subQ14=sQuery(id+"F12.wireOp",EDGE,"E72.1");var subQ16=sQuery(id+"F12.wireOp",EDGE,"E74.1");var subQ18=sQuery(id+"F12.wireOp",EDGE,"E74.8");Q0=qUnion([makeQuery(id+"F12.imprint","IMPRINT",FACE,{"disambiguationData":[TD([[makeQuery(id+"F12.imprint","IMPRINT",EDGE,{"derivedFrom":subQ7}),1.0]])]}),makeQuery(id+"F12.imprint","IMPRINT",FACE,{"disambiguationData":[TD([[makeQuery(id+"F12.imprint","IMPRINT",EDGE,{"derivedFrom":subQ14}),1.0]])]}),makeQuery(id+"F12.imprint","IMPRINT",FACE,{"disambiguationData":[TD([[makeQuery(id+"F12.imprint","IMPRINT",EDGE,{"derivedFrom":subQ16}),1.0]])]}),makeQuery(id+"F12.imprint","IMPRINT",FACE,{"disambiguationData":[TD([[makeQuery(id+"F12.imprint","IMPRINT",EDGE,{"derivedFrom":subQ18}),-1.0]])]})]);}
            var Q1;
            Q1=makeQuery(id+"F5.boolean.opBoolean","SPLIT",FACE,{"disambiguationData":[TD([makeQuery(id+"F5.opExtrude","SWEPT_FACE",FACE,{"disambiguationData":[OSD([sQuery(id+"F4.wireOp",EDGE,"E41")])]})])],"derivedFrom":makeQuery(id+"F3.boolean.opBoolean","COPY",FACE,{"derivedFrom":makeQuery(id+"F3.opExtrude","CAP_FACE",FACE,{"disambiguationData":[OSD([sQuery(id+"F0.wireOp",EDGE,"E25.0"),sQuery(id+"F0.wireOp",EDGE,"E25.1"),sQuery(id+"F0.wireOp",EDGE,"E25.2"),sQuery(id+"F0.wireOp",EDGE,"E25.3"),sQuery(id+"F0.wireOp",EDGE,"E25.4"),sQuery(id+"F0.wireOp",EDGE,"E25.5"),sQuery(id+"F0.wireOp",EDGE,"E25.6"),sQuery(id+"F0.wireOp",EDGE,"E25.7")])],"isStart":false})})});
            extrude(context, id + "F13", {"entities" : qUnion([Q0]), "operationType" : NewBodyOperationType.REMOVE, "endBound" : BoundingType.UP_TO_SURFACE, "endBoundEntityFace" : qUnion([Q1]), "depth" : 25 * mm});
        }
        {
            var Q0;
            Q0=makeQuery(id+"F3.boolean.opBoolean","COPY",EDGE,{"derivedFrom":makeQuery(id+"F3.opExtrude","CAP_EDGE",EDGE,{"disambiguationData":[OSD([sQuery(id+"F0.wireOp",EDGE,"E25.6")])],"isStart":false})});
            var Q1;
            Q1=makeQuery(id+"F8.boolean.opBoolean","INTERSECT",EDGE,{"derivedFrom":[makeQuery(id+"F5.opExtrude","SWEPT_FACE",FACE,{"disambiguationData":[OSD([sQuery(id+"F4.wireOp",EDGE,"E30")])]}),makeQuery(id+"F8.opExtrude","CAP_FACE",FACE,{"disambiguationData":[OSD([sQuery(id+"F7.wireOp",EDGE,"E67")])],"isStart":false})]});
            var Q2;
            Q2=makeQuery(id+"F8.boolean.opBoolean","INTERSECT",EDGE,{"disambiguationData":[OD(1.0)],"derivedFrom":[makeQuery(id+"F5.opExtrude","SWEPT_FACE",FACE,{"disambiguationData":[OSD([sQuery(id+"F4.wireOp",EDGE,"E30")])]}),makeQuery(id+"F8.opExtrude","SWEPT_FACE",FACE,{"disambiguationData":[OSD([sQuery(id+"F7.wireOp",EDGE,"E67")])]})]});
            var Q3;
            {var subQ0=sQuery(id+"F4.wireOp",EDGE,"E30");Q3=makeQuery(id+"F8.boolean.opBoolean","SPLIT",EDGE,{"disambiguationData":[TD([makeQuery(id+"F5.opExtrude","SWEPT_FACE",FACE,{"disambiguationData":[OSD([sQuery(id+"F4.wireOp",EDGE,"E35.filletArc")])]})])],"derivedFrom":makeQuery(id+"F5.opExtrude","CAP_EDGE",EDGE,{"disambiguationData":[OSD([subQ0])],"isStart":false})});}
            var Q4;
            {var subQ0=sQuery(id+"F0.wireOp",EDGE,"E25.7");var subQ1=sQuery(id+"F0.wireOp",EDGE,"E25.1");var subQ2=sQuery(id+"F0.wireOp",EDGE,"E25.6");var subQ3=sQuery(id+"F0.wireOp",EDGE,"E25.5");var subQ4=sQuery(id+"F0.wireOp",EDGE,"E25.4");var subQ5=sQuery(id+"F0.wireOp",EDGE,"E25.0");var subQ6=sQuery(id+"F0.wireOp",EDGE,"E25.2");var subQ7=sQuery(id+"F0.wireOp",EDGE,"E25.3");Q4=makeQuery(id+"F8.boolean.opBoolean","INTERSECT",EDGE,{"derivedFrom":[makeQuery(id+"F5.boolean.opBoolean","SPLIT",FACE,{"disambiguationData":[TD([makeQuery(id+"F2.opExtrude","SWEPT_FACE",FACE,{"disambiguationData":[OSD([subQ5])]})])],"derivedFrom":makeQuery(id+"F3.boolean.opBoolean","COPY",FACE,{"derivedFrom":makeQuery(id+"F3.opExtrude","CAP_FACE",FACE,{"disambiguationData":[OSD([subQ5,subQ1,subQ6,subQ7,subQ4,subQ3,subQ2,subQ0])],"isStart":false})})}),makeQuery(id+"F8.opExtrude","SWEPT_FACE",FACE,{"disambiguationData":[OSD([sQuery(id+"F7.wireOp",EDGE,"E67")])]})]});}
            var Q5;
            Q5=makeQuery(id+"F8.boolean.opBoolean","INTERSECT",EDGE,{"disambiguationData":[OD(0.0)],"derivedFrom":[makeQuery(id+"F5.opExtrude","SWEPT_FACE",FACE,{"disambiguationData":[OSD([sQuery(id+"F4.wireOp",EDGE,"E30")])]}),makeQuery(id+"F8.opExtrude","SWEPT_FACE",FACE,{"disambiguationData":[OSD([sQuery(id+"F7.wireOp",EDGE,"E67")])]})]});
            fillet(context, id + "F14", {"entities" : qUnion([Q0, Q1, Q2, Q3, Q4, Q5]), "radius" : 3 * mm, "tangentPropagation" : true, "allowEdgeOverflow" : false});
        }
        {
            var Q0;
            Q0=makeQuery(id+"F1.opExtrude","CAP_EDGE",EDGE,{"disambiguationData":[OSD([sQuery(id+"F0.wireOp",EDGE,"E1.bottom")])],"isStart":false});
            fillet(context, id + "F15", {"entities" : qUnion([Q0]), "radius" : 2 * mm, "tangentPropagation" : true, "allowEdgeOverflow" : false});
        }
        {
            var Q0;
            {var subQ0=sQuery(id+"F0.wireOp",EDGE,"E22.filletArc");var subQ1=sQuery(id+"F0.wireOp",EDGE,"E7");var subQ2=sQuery(id+"F0.wireOp",EDGE,"E6");var subQ3=sQuery(id+"F0.wireOp",EDGE,"E5");var subQ4=sQuery(id+"F0.wireOp",EDGE,"E4");var subQ5=sQuery(id+"F0.wireOp",EDGE,"E1.bottom");var subQ6=sQuery(id+"F0.wireOp",EDGE,"E21.filletArc");var subQ7=sQuery(id+"F0.wireOp",EDGE,"E1.top");var subQ8=sQuery(id+"F0.wireOp",EDGE,"E1.left");var subQ9=sQuery(id+"F0.wireOp",EDGE,"E1.right");var subQ10=sQuery(id+"F0.wireOp",EDGE,"E23.filletArc");var subQ11=sQuery(id+"F0.wireOp",EDGE,"E24.filletArc");Q0=makeQuery(id+"F2.boolean.opBoolean","SPLIT",FACE,{"disambiguationData":[TD([makeQuery(id+"F1.opExtrude","SWEPT_FACE",FACE,{"disambiguationData":[OSD([subQ5])]})])],"derivedFrom":makeQuery(id+"F1.opExtrude","CAP_FACE",FACE,{"disambiguationData":[OSD([subQ5,subQ7,subQ8,subQ9,subQ4,subQ3,subQ2,subQ1,subQ6,subQ0,subQ10,subQ11])],"isStart":true})});}
            var sketch = newSketch(context, id + "F16", { "sketchPlane" : qUnion([Q0])});
            skLineSegment(sketch, "E79", {"start": v(0, 74.25) * mm, "end": v(0, 104.25) * mm});
            skPoint(sketch, "E79.endSnap0", {"position": v(0, 74.25) * mm});
            skLineSegment(sketch, "E80", {"start": v(0, 104.25) * mm, "end": v(0, 74.25) * mm});
            skLineSegment(sketch, "E81", {"start": v(0, 74.25) * mm, "end": v(-32.14, 74.25) * mm});
            skCircle(sketch, "E82", {"center": v(0, 104.25) * mm, "radius": 1.51 * mm});
            skLineSegment(sketch, "E83", {"start": v(0, 74.25) * mm, "end": v(32.14, 74.25) * mm});
            skLineSegment(sketch, "E84", {"start": v(32.14, 74.25) * mm, "end": v(13.04, 93.34) * mm});
            skLineSegment(sketch, "E85", {"start": v(13.04, 93.34) * mm, "end": v(13.04, 104.25) * mm});
            skLineSegment(sketch, "E86", {"start": v(13.04, 104.25) * mm, "end": v(13.04, 93.34) * mm});
            skLineSegment(sketch, "E87", {"start": v(-32.14, 74.25) * mm, "end": v(-13.04, 93.34) * mm});
            skLineSegment(sketch, "E88", {"start": v(-13.04, 93.34) * mm, "end": v(-13.04, 104.25) * mm});
            skLineSegment(sketch, "E89", {"start": v(-13.04, 104.25) * mm, "end": v(-13.04, 93.34) * mm});
            skLineSegment(sketch, "E90", {"start": v(13.04, 93.34) * mm, "end": v(32.14, 74.25) * mm});
            skLineSegment(sketch, "E91", {"start": v(-13.04, 93.34) * mm, "end": v(-32.14, 74.25) * mm});
            skArc(sketch, "E92", {"start": v(13.04, 104.25) * mm, "mid": v(0, 117.3) * mm, "end": v(-13.04, 104.25) * mm});
            skLineSegment(sketch, "E93", {"start": v(-13.04, 93.34) * mm, "end": v(0, 93.34) * mm});
            skPoint(sketch, "E93.endSnap0", {"position": v(0, 89.25) * mm});
            skLineSegment(sketch, "E94", {"start": v(0, 93.34) * mm, "end": v(13.04, 93.34) * mm});
            skLineSegment(sketch, "E95", {"start": v(-74.25, 0) * mm, "end": v(74.25, 0) * mm, "construction": true});
            skLineSegment(sketch, "E96", {"start": v(74.25, 0) * mm, "end": v(-74.25, 0) * mm, "construction": true});
            skArc(sketch, "E97.MirrorCS", {"start": v(13.04, -104.25) * mm, "mid": v(0, -117.3) * mm, "end": v(-13.04, -104.25) * mm});
            skCircle(sketch, "E98.MirrorC", {"center": v(0, -104.25) * mm, "radius": 1.51 * mm});
            skLineSegment(sketch, "E99.MirrorCS", {"start": v(-13.04, -93.34) * mm, "end": v(-13.04, -104.25) * mm});
            skLineSegment(sketch, "E100.MirrorCS", {"start": v(-32.14, -74.25) * mm, "end": v(-13.04, -93.34) * mm});
            skLineSegment(sketch, "E101.MirrorCS", {"start": v(32.14, -74.25) * mm, "end": v(13.04, -93.34) * mm});
            skLineSegment(sketch, "E102.MirrorCS", {"start": v(13.04, -93.34) * mm, "end": v(13.04, -104.25) * mm});
            skLineSegment(sketch, "E103.MirrorCS", {"start": v(0, -74.25) * mm, "end": v(0, -104.25) * mm});
            skLineSegment(sketch, "E104.MirrorCS", {"start": v(-13.04, -93.34) * mm, "end": v(-32.14, -74.25) * mm});
            skLineSegment(sketch, "E105.MirrorCS", {"start": v(13.04, -93.34) * mm, "end": v(32.14, -74.25) * mm});
            skLineSegment(sketch, "E106.MirrorCS", {"start": v(-13.04, -104.25) * mm, "end": v(-13.04, -93.34) * mm});
            skPoint(sketch, "E107.MirrorP", {"position": v(0, -89.25) * mm});
            skLineSegment(sketch, "E108.MirrorCS", {"start": v(13.04, -104.25) * mm, "end": v(13.04, -93.34) * mm});
            skPoint(sketch, "E109.MirrorP", {"position": v(0, -74.25) * mm});
            skLineSegment(sketch, "E110.MirrorCS", {"start": v(0, -74.25) * mm, "end": v(32.14, -74.25) * mm});
            skLineSegment(sketch, "E111.MirrorCS", {"start": v(0, -74.25) * mm, "end": v(-32.14, -74.25) * mm});
            skLineSegment(sketch, "E112.MirrorCS", {"start": v(0, -104.25) * mm, "end": v(0, -74.25) * mm});
            skLineSegment(sketch, "E113.MirrorCS", {"start": v(-13.04, -93.34) * mm, "end": v(0, -93.34) * mm});
            skLineSegment(sketch, "E114.MirrorCS", {"start": v(0, -93.34) * mm, "end": v(13.04, -93.34) * mm});
            skSolve(sketch);
        }
        {
            var Q0;
            Q0 = qSketchRegion(id + "F16", true);
            extrude(context, id + "F17", {"entities" : qUnion([Q0]), "oppositeDirection" : true, "depth" : 25 * mm});
        }
    });
